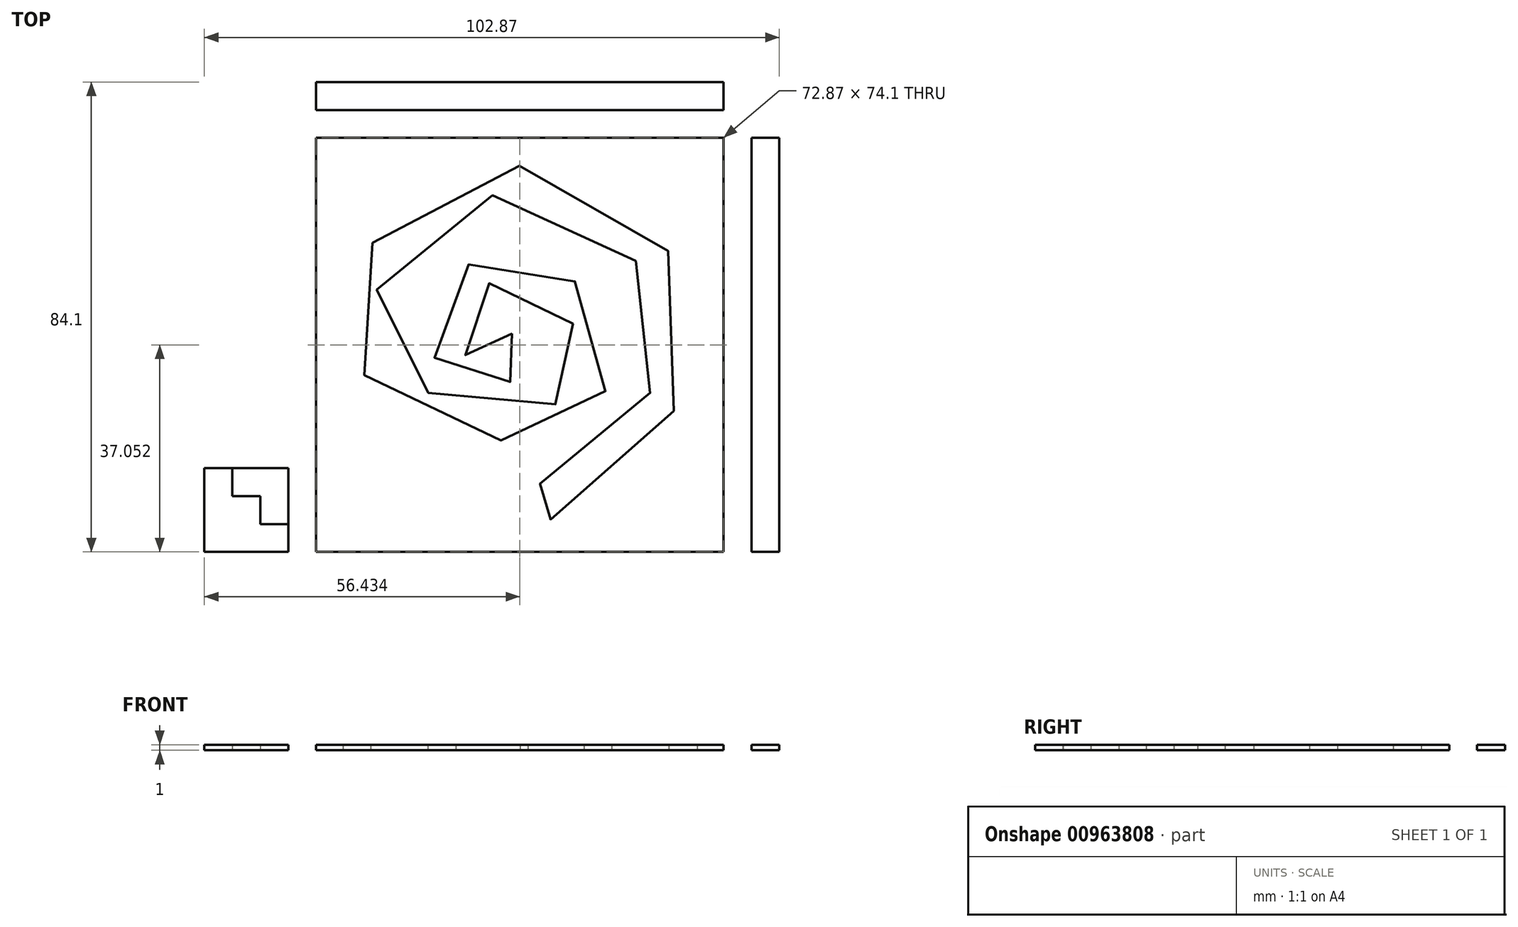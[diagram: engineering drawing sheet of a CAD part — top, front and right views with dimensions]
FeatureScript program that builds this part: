
annotation { "Feature Type Name" : "Feature", "Feature Type Description" : "" }
export const myFeature = defineFeature(function(context is Context, id is Id, definition is map)
    precondition{}
    {
        {
            var Q0;
            Q0=qCreatedBy(makeId("Top.planeOp"),FACE);
            var sketch = newSketch(context, id + "F0", { "sketchPlane" : qUnion([Q0])});
            skLineSegment(sketch, "E0.bottom", {"start": v(47.87, 35) * mm, "end": v(42.87, 35) * mm});
            skLineSegment(sketch, "E0.top", {"start": v(47.87, -39.1) * mm, "end": v(42.87, -39.1) * mm});
            skLineSegment(sketch, "E0.left", {"start": v(47.87, 35) * mm, "end": v(47.87, -39.1) * mm});
            skLineSegment(sketch, "E0.right", {"start": v(42.87, 35) * mm, "end": v(42.87, -39.1) * mm});
            skLineSegment(sketch, "E1.bottom", {"start": v(-35, 35) * mm, "end": v(37.87, 35) * mm});
            skLineSegment(sketch, "E1.top", {"start": v(-35, -39.1) * mm, "end": v(37.87, -39.1) * mm});
            skLineSegment(sketch, "E1.left", {"start": v(-35, 35) * mm, "end": v(-35, -39.1) * mm});
            skLineSegment(sketch, "E1.right", {"start": v(37.87, 35) * mm, "end": v(37.87, -39.1) * mm});
            skFitSpline(sketch, "E2", {"points": [v(0, 0) * mm, v(-5, -5) * mm, v(-10, 0) * mm, v(0, 10) * mm, v(12.87, -4.1) * mm, v(2.87, -14.1) * mm, v(-25, 0) * mm, v(0, 25) * mm, v(27.87, -4.1) * mm, v(2.87, -29.1) * mm, v(2.87, -34.1) * mm, v(32.87, -4.1) * mm, v(0, 30) * mm, v(-30, 0) * mm, v(2.87, -19.1) * mm, v(17.87, -4.1) * mm, v(0, 15) * mm, v(-15, 0) * mm, v(-5, -10) * mm, v(2.87, -4.1) * mm, v(0, 0) * mm]});
            skLineSegment(sketch, "E3", {"start": v(32.87, -4.1) * mm, "end": v(27.87, -4.1) * mm, "construction": true});
            skLineSegment(sketch, "E4", {"start": v(2.87, -34.1) * mm, "end": v(2.87, -29.1) * mm, "construction": true});
            skLineSegment(sketch, "E5", {"start": v(0, 30) * mm, "end": v(0, 25) * mm, "construction": true});
            skLineSegment(sketch, "E6", {"start": v(-25, 0) * mm, "end": v(-30, 0) * mm, "construction": true});
            skLineSegment(sketch, "E7", {"start": v(2.87, -14.1) * mm, "end": v(2.87, -19.1) * mm, "construction": true});
            skLineSegment(sketch, "E8", {"start": v(2.87, -4.1) * mm, "end": v(0, 0) * mm, "construction": true});
            skLineSegment(sketch, "E9", {"start": v(-5, -5) * mm, "end": v(-5, -10) * mm, "construction": true});
            skLineSegment(sketch, "E10", {"start": v(-10, 0) * mm, "end": v(-15, 0) * mm, "construction": true});
            skLineSegment(sketch, "E11", {"start": v(0, 15) * mm, "end": v(0, 10) * mm, "construction": true});
            skLineSegment(sketch, "E12", {"start": v(12.87, -4.1) * mm, "end": v(17.87, -4.1) * mm, "construction": true});
            skLineSegment(sketch, "E13", {"start": v(0, 0) * mm, "end": v(-10, 0) * mm, "construction": true});
            skLineSegment(sketch, "E14", {"start": v(-15, 0) * mm, "end": v(-25, 0) * mm, "construction": true});
            skLineSegment(sketch, "E15", {"start": v(17.87, -4.1) * mm, "end": v(27.87, -4.1) * mm, "construction": true});
            skLineSegment(sketch, "E16", {"start": v(0, 0) * mm, "end": v(0, 10) * mm, "construction": true});
            skLineSegment(sketch, "E17", {"start": v(0, 15) * mm, "end": v(0, 25) * mm, "construction": true});
            skLineSegment(sketch, "E18", {"start": v(2.87, -19.1) * mm, "end": v(2.87, -29.1) * mm, "construction": true});
            skLineSegment(sketch, "E19", {"start": v(2.87, -4.1) * mm, "end": v(12.87, -4.1) * mm, "construction": true});
            skLineSegment(sketch, "E20", {"start": v(2.87, -4.1) * mm, "end": v(2.87, -14.1) * mm, "construction": true});
            skLineSegment(sketch, "E21", {"start": v(-5, -5) * mm, "end": v(-5, 0) * mm, "construction": true});
            skLineSegment(sketch, "E22", {"start": v(-55, -24.1) * mm, "end": v(-50, -24.1) * mm});
            skLineSegment(sketch, "E23", {"start": v(-50, -24.1) * mm, "end": v(-45, -24.1) * mm});
            skLineSegment(sketch, "E24", {"start": v(-40, -24.1) * mm, "end": v(-45, -24.1) * mm});
            skLineSegment(sketch, "E25", {"start": v(-40, -24.1) * mm, "end": v(-40, -29.1) * mm});
            skLineSegment(sketch, "E26", {"start": v(-40, -29.1) * mm, "end": v(-40, -34.1) * mm});
            skLineSegment(sketch, "E27", {"start": v(-40, -34.1) * mm, "end": v(-40, -39.1) * mm});
            skLineSegment(sketch, "E28", {"start": v(-40, -39.1) * mm, "end": v(-45, -39.1) * mm});
            skLineSegment(sketch, "E29", {"start": v(-45, -39.1) * mm, "end": v(-50, -39.1) * mm});
            skLineSegment(sketch, "E30", {"start": v(-50, -39.1) * mm, "end": v(-55, -39.1) * mm});
            skLineSegment(sketch, "E31", {"start": v(-55, -39.1) * mm, "end": v(-55, -34.1) * mm});
            skLineSegment(sketch, "E32", {"start": v(-55, -34.1) * mm, "end": v(-55, -29.1) * mm});
            skLineSegment(sketch, "E33", {"start": v(-55, -29.1) * mm, "end": v(-55, -24.1) * mm});
            skLineSegment(sketch, "E34", {"start": v(-50, -24.1) * mm, "end": v(-50, -29.1) * mm});
            skLineSegment(sketch, "E35", {"start": v(-50, -29.1) * mm, "end": v(-45, -29.1) * mm});
            skLineSegment(sketch, "E36", {"start": v(-45, -29.1) * mm, "end": v(-45, -34.1) * mm});
            skLineSegment(sketch, "E37", {"start": v(-45, -34.1) * mm, "end": v(-40, -34.1) * mm});
            skLineSegment(sketch, "E38", {"start": v(-30, 0) * mm, "end": v(-35, 0) * mm, "construction": true});
            skLineSegment(sketch, "E39", {"start": v(0, 30) * mm, "end": v(0, 35) * mm, "construction": true});
            skLineSegment(sketch, "E40", {"start": v(2.87, -34.1) * mm, "end": v(2.87, -39.1) * mm, "construction": true});
            skLineSegment(sketch, "E41", {"start": v(32.87, -4.1) * mm, "end": v(37.87, -4.1) * mm, "construction": true});
            skLineSegment(sketch, "E42.bottom", {"start": v(-35, 45) * mm, "end": v(37.87, 45) * mm});
            skLineSegment(sketch, "E42.top", {"start": v(-35, 40) * mm, "end": v(37.87, 40) * mm});
            skLineSegment(sketch, "E42.left", {"start": v(-35, 45) * mm, "end": v(-35, 40) * mm});
            skLineSegment(sketch, "E42.right", {"start": v(37.87, 45) * mm, "end": v(37.87, 40) * mm});
            skLineSegment(sketch, "E43", {"start": v(37.87, 40) * mm, "end": v(37.87, 35) * mm, "construction": true});
            skLineSegment(sketch, "E44", {"start": v(37.87, 35) * mm, "end": v(42.87, 35) * mm, "construction": true});
            skLineSegment(sketch, "E45", {"start": v(-40, -39.1) * mm, "end": v(-35, -39.1) * mm, "construction": true});
            skSolve(sketch);
        }
        {
            var Q0;
            Q0=makeQuery(id+"F0.imprint","IMPRINT",FACE,{"disambiguationData":[TD([[makeQuery(id+"F0.imprint","IMPRINT",EDGE,{"derivedFrom":sQuery(id+"F0.wireOp",EDGE,"E2")}),1.0]])]});
            var Q1;
            Q1=makeQuery(id+"F0.imprint","IMPRINT",FACE,{"disambiguationData":[TD([[makeQuery(id+"F0.imprint","IMPRINT",EDGE,{"derivedFrom":sQuery(id+"F0.wireOp",EDGE,"E42.bottom")}),-1.0]])]});
            var Q2;
            Q2=makeQuery(id+"F0.imprint","IMPRINT",FACE,{"disambiguationData":[TD([[makeQuery(id+"F0.imprint","IMPRINT",EDGE,{"derivedFrom":sQuery(id+"F0.wireOp",EDGE,"E0.bottom")}),1.0]])]});
            var Q3;
            Q3=makeQuery(id+"F0.imprint","IMPRINT",FACE,{"disambiguationData":[TD([[makeQuery(id+"F0.imprint","IMPRINT",EDGE,{"derivedFrom":sQuery(id+"F0.wireOp",EDGE,"E22")}),-1.0]])]});
            extrude(context, id + "F1", {"entities" : qUnion([Q0, Q1, Q2, Q3]), "depth" : 1 * mm, "offsetDistance" : 25 * mm});
        }
        {
            var Q0;
            Q0=makeQuery(id+"F0.imprint","IMPRINT",FACE,{"disambiguationData":[TD([[makeQuery(id+"F0.imprint","IMPRINT",EDGE,{"derivedFrom":sQuery(id+"F0.wireOp",EDGE,"E1.bottom")}),-1.0]])]});
            var Q1;
            Q1=makeQuery(id+"F0.imprint","IMPRINT",FACE,{"disambiguationData":[TD([[makeQuery(id+"F0.imprint","IMPRINT",EDGE,{"derivedFrom":sQuery(id+"F0.wireOp",EDGE,"E23")}),-1.0]])]});
            extrude(context, id + "F2", {"entities" : qUnion([Q0, Q1]), "depth" : 1 * mm, "offsetDistance" : 25 * mm});
        }
    });
